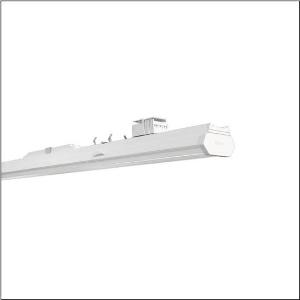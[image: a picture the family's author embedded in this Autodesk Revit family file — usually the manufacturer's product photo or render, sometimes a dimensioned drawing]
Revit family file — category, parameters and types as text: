
# Revit family: licross_r__21_protected_mo_52td1bcn485g_f119
name_source: partatom
category: Lighting Fixtures
units: mm (PartAtom-declared; Revit-internal decimal feet)

## family parameters
Cut with Voids When Loaded = No
Host = Face
Light Source = No
Part Type = Normal
Room Calculation Point = No
Round Connector Dimension = Use Diameter
Shared = No

## types (1)
- --- (1 x LED, 8570 lm, 50.4 W, 4000K)
    Apparent Load = 50 VA
    CIE Flux Codes = 54 82 95 97 100
    Color Rendering = 80
    Color Temperature = 4000K
    Default Elevation = 1800 mm
    Description = Licross® 21 Protected MO, luminaire insert, of sheet steel, galvanised, coil coated, white, length: 1.500mm, width: 90mm, height: 103mm, LED rated luminous flux: 8.570lm, light colour: 840, control gear: ON/OFF Multilumen, CLOi, control gear: ECG Multilumen, with plug, 3-pole, with phase selection, mains connection: 220..240V, AC, 50/60Hz, start of lifetime: 50W, end of service life: 61W, halogen-free wiring, primary optical cover: cover, of PMMA, light emission: direct distribution, primary light characteristic: symmetric, protection rating (complete): IP54, insulation class (complete): insulation class I (protective earthing), certification: CE, ENEC, VDE, UKCA, protection symbol: D if used in an environment with non-conductive dust loads with corresponding accessories, impact resistance: IK06, permissible ambient temperature for indoor applications: -35..+45°C, corresponds to IFS (International Featured Standards) requirements for safety and quality in the food industry, reducing of maximum allowable ambient temperature of 5°C with ceiling mounting, LABS conformity tested according to VDMA 24364:2018-05, packaging unit: 1 piece
    Height = 92 mm
    Lamp = 1 x LED
    Lamp Light Flux = 8570 lm
    Lamp Power = 50.4 W
    Lamp count = 1
    Length = 1500 mm
    Luminous efficacy = 170 lm/W
    Manufacturer = Siteco
    ModVariant = No
    Model = 52TD1BCN485G
    Mounting Place = Ceiling
    Mounting Type = Pendant
    Number of Poles = 1
    OnlyDefault = Yes
    Power Factor = 1
    Product Name = Licross® 21 Protected MO
    Product group = luminaire insert
    ProductGroupID = 901
    Protection Class = Protection class I
    Protection Degree = IP 54
    RLX_Detail_Level = 1
    RLX_Emergency_Light_Flux = 0 lm
    RLX_Emergency_Type = 0
    RLX_Emergency_Type_DB = No
    RlxData = <blob elided: 22049 chars, md5=80b27619>
    Socket = socket
    Standby Power = 0 W
    System Light Flux = 8570 lm
    System Power = 50 W
    Type Comments = factory setting: luminous flux: 100 % | (A | C | E) | 117 mA
    Type Image = l_1256148.jpg
    URL = http://relux.com
    VarID = @adj_041601
    Voltage = 0 V
    Weight = 0.00 kg
    Width = 88 mm

## geometry (parser evidence)
native form markers: Blend x4, Sweep x9
no freeform markers — native parametric forms only
